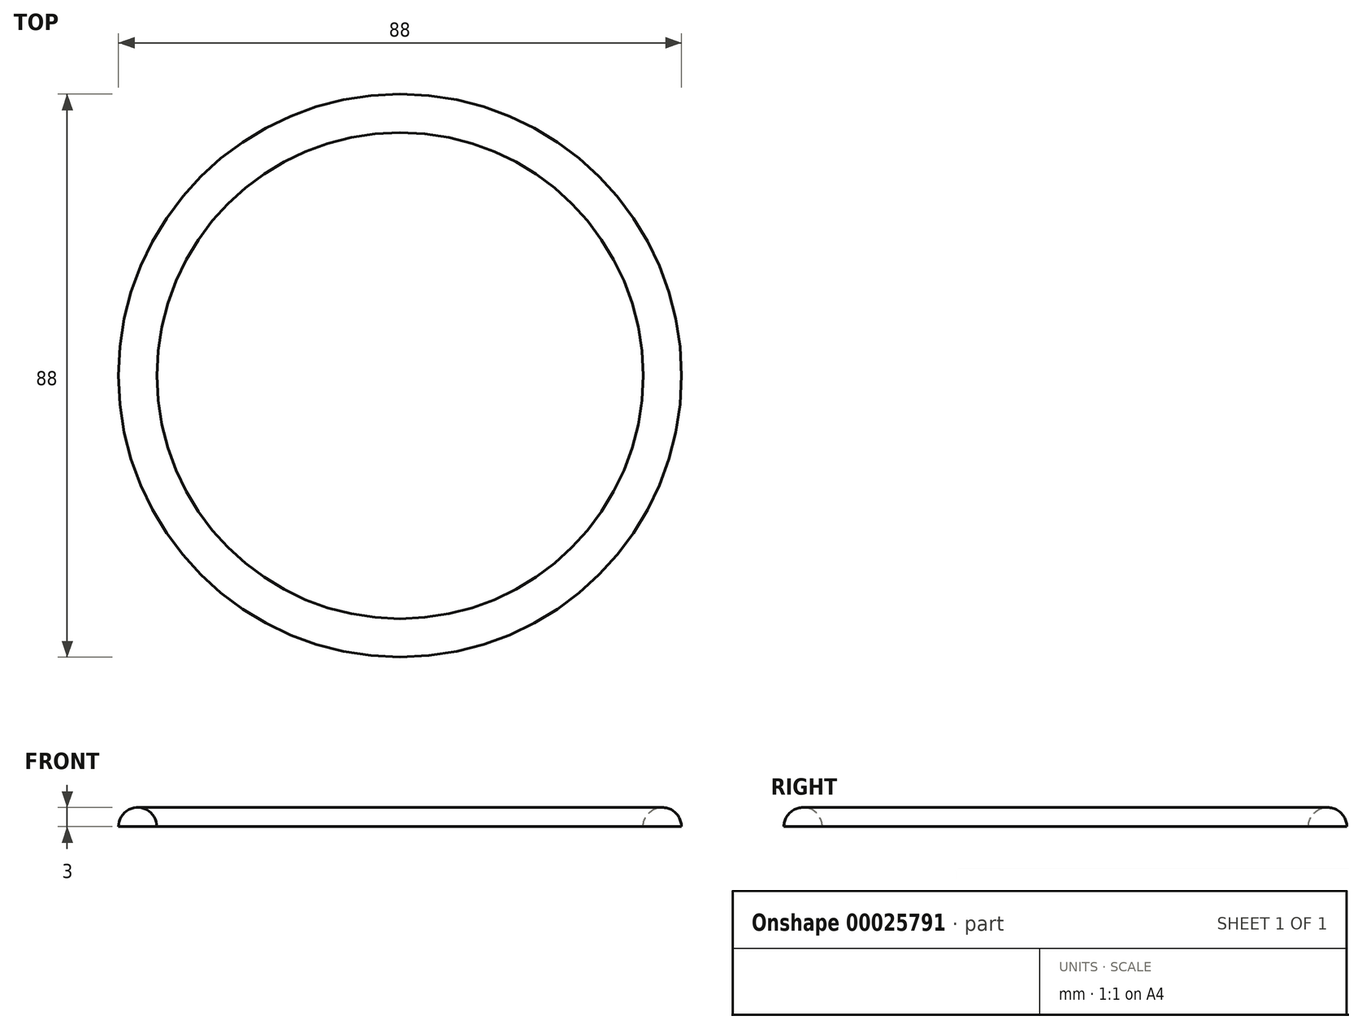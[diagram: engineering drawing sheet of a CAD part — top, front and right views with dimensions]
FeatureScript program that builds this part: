
annotation { "Feature Type Name" : "Feature", "Feature Type Description" : "" }
export const myFeature = defineFeature(function(context is Context, id is Id, definition is map)
    precondition{}
    {
        {
            var Q0;
            Q0=qCreatedBy(makeId("Front.planeOp"),FACE);
            var sketch = newSketch(context, id + "F0", { "sketchPlane" : qUnion([Q0])});
            skLineSegment(sketch, "E0", {"start": v(0, 0) * mm, "end": v(0, 33.02) * mm, "construction": true});
            skLineSegment(sketch, "E1", {"start": v(0, 0) * mm, "end": v(-38, 0) * mm, "construction": true});
            skLineSegment(sketch, "E2", {"start": v(-38, 0) * mm, "end": v(-44, 0) * mm});
            skArc(sketch, "E3", {"start": v(-38, 0) * mm, "mid": v(-41, 3) * mm, "end": v(-44, 0) * mm});
            skSolve(sketch);
        }
        {
            var Q0;
            Q0=makeQuery(id+"F0.imprint","IMPRINT",FACE,{"disambiguationData":[TD([[makeQuery(id+"F0.imprint","IMPRINT",EDGE,{"derivedFrom":sQuery(id+"F0.wireOp",EDGE,"E2")}),-1.0]])]});
            var Q1;
            Q1=sQuery(id+"F0.wireOp",EDGE,"E0");
            revolve(context, id + "F1", {"entities" : qUnion([Q0]), "axis" : qUnion([Q1]), "revolveType" : RevolveType.FULL});
        }
    });
